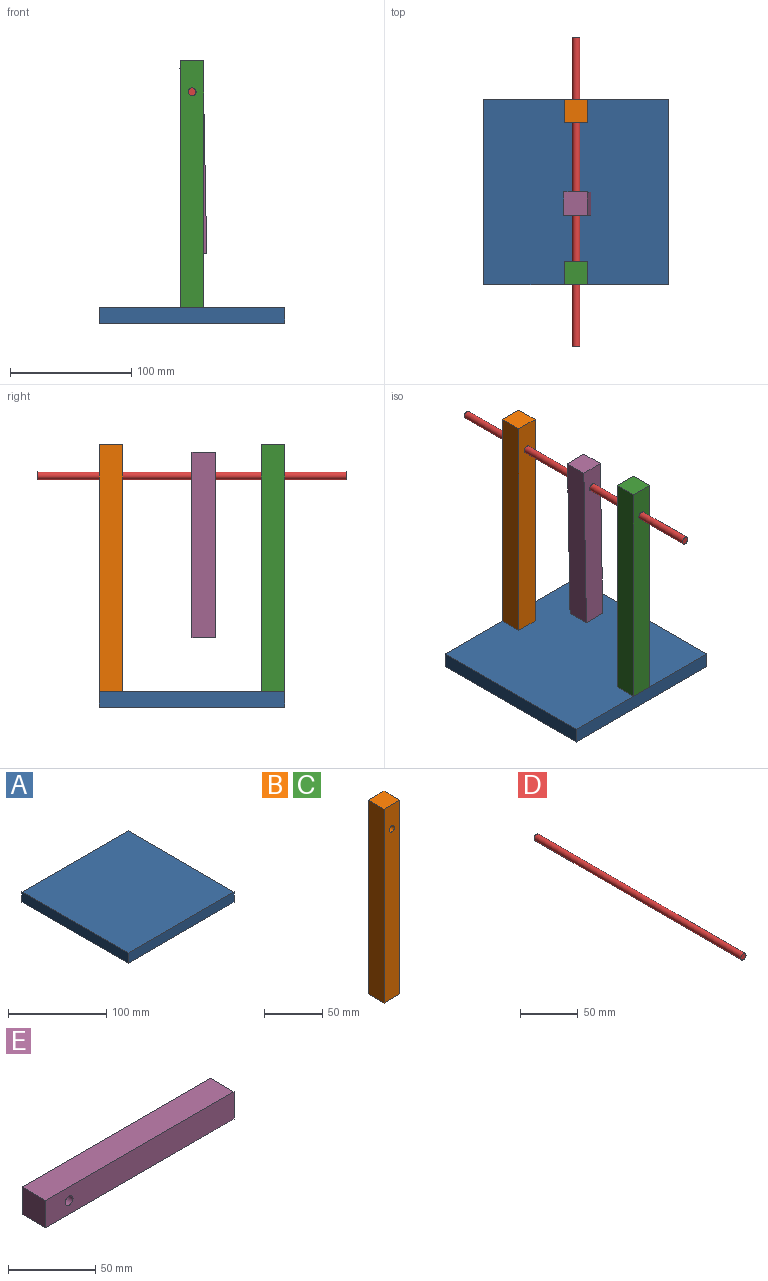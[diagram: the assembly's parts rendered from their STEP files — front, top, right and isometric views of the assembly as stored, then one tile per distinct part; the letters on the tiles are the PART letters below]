
ASSEMBLY  parts=5 mates=4
PART A: 6 faces, bbox 152.4x152.4x12.7 mm
  f0: plane 152.4x12.7mm, normal (0,1,0), area 1935.5mm2, adj f1,f3,f4,f5
  f1: plane 152.4x12.7mm, normal (-1,0,0), area 1935.5mm2, adj f0,f2,f4,f5
  f2: plane 152.1x12.7mm, normal (0,-1,0), area 1931.7mm2, adj f1,f3,f4,f5
  f3: plane 152.4x12.7mm, normal (1,0,0), area 1935.5mm2, adj f0,f2,f4,f5
  f4: plane 152.4x152.4mm, normal (0,0,1), area 23203.2mm2, adj f0,f1,f2,f3
  f5: plane 152.4x152.4mm, normal (0,0,-1), area 23203.2mm2, adj f0,f1,f2,f3
PART B: 7 faces, bbox 19.1x19.1x203.2 mm
  f0: plane 203.2x19.05mm, normal (-1,0,0), area 3871mm2, adj f1,f3,f4,f5
  f1: plane 19.05x19.05mm, normal (0,0,-1), area 362.9mm2, adj f0,f2,f4,f5
  f2: plane 203.2x19.05mm, normal (1,0,0), area 3871mm2, adj f1,f3,f4,f5
  f3: plane 19.05x19.05mm, normal (0,0,1), area 362.9mm2, adj f0,f2,f4,f5
  f4: plane 203.2x19.05mm, normal (0,-1,0), area 3839.3mm2, adj f0,f1,f2,f3,f6
  f5: plane 203.2x19.05mm, normal (0,1,0), area 3839.3mm2, adj f0,f1,f2,f3,f6
  f6: cylinder r=3.17mm len=19.05mm, axis (0,-1,0), area 380mm2, adj f4,f5
PART C: same geometry as B
PART D: 3 faces, bbox 6.4x254x6.4 mm
  f0: cylinder r=3.17mm len=254mm, axis (0,1,0), area 5067.1mm2, adj f1,f2
  f1: plane 6.35x6.35mm, normal (0,-1,0), area 31.7mm2, adj f0
  f2: plane 6.35x6.35mm, normal (0,1,0), area 31.7mm2, adj f0
PART E: 7 faces, bbox 152.4x19.1x19.1 mm
  f0: plane 19.05x19.05mm, normal (-1,0,0), area 362.9mm2, adj f1,f3,f4,f5
  f1: plane 152.4x19.05mm, normal (0,0,-1), area 2903.2mm2, adj f0,f2,f4,f5
  f2: plane 19.05x19.05mm, normal (1,0,0), area 362.9mm2, adj f1,f3,f4,f5
  f3: plane 152.4x19.05mm, normal (0,0,1), area 2903.2mm2, adj f0,f2,f4,f5
  f4: plane 152.4x19.05mm, normal (0,-1,0), area 2871.6mm2, adj f0,f1,f2,f3,f6
  f5: plane 152.4x19.05mm, normal (0,1,0), area 2871.6mm2, adj f0,f1,f2,f3,f6
  f6: cylinder r=3.17mm len=19.05mm, axis (0,-1,0), area 380mm2, adj f4,f5
PLACE A t=(0.08,-3.52,-11.25)mm fixed
PLACE B t=(-9.44,72.98,102.74)mm
PLACE C t=(-9.3,-60.37,102.74)mm
PLACE D t=(0.08,123.78,179.25)mm
PLACE E rot(axis=(0,1,0),88.9deg) t=(-9.81,-3.22,198.11)mm
MATE fastened C.f1 <-> A.f4  axis (0,0,-1) through (0.23,-79.42,1.45)mm
MATE fastened B.f1 <-> A.f4  axis (0,0,-1) through (0.08,72.98,1.45)mm
MATE revolute D.f0 <-> B.f6  axis (0,1,0) through (0.08,123.78,179.25)mm
MATE revolute E.f6 <-> D.f0  axis (0,1,0) through (0.08,-3.22,179.25)mm
